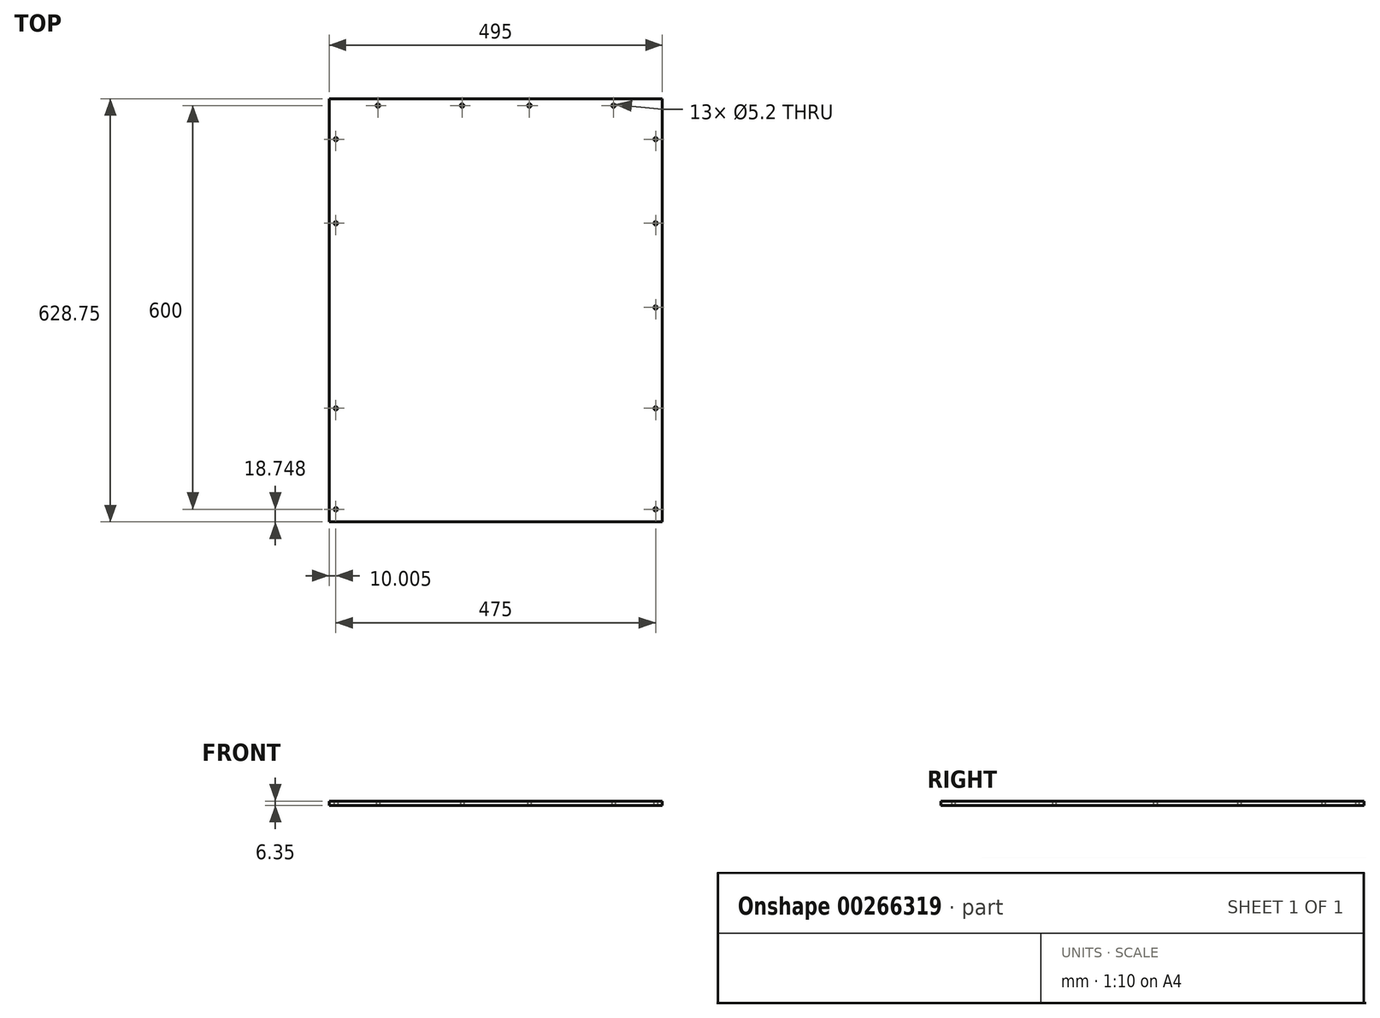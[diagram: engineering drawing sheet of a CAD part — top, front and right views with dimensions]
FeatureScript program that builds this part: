
annotation { "Feature Type Name" : "Feature", "Feature Type Description" : "" }
export const myFeature = defineFeature(function(context is Context, id is Id, definition is map)
    precondition{}
    {
        {
            var Q0;
            Q0=qCreatedBy(makeId("Top.planeOp"),FACE);
            var sketch = newSketch(context, id + "F0", { "sketchPlane" : qUnion([Q0])});
            skLineSegment(sketch, "E0.bottom", {"start": v(-53.27, -32.57) * mm, "end": v(441.73, -32.57) * mm});
            skLineSegment(sketch, "E0.top", {"start": v(-53.27, 596.18) * mm, "end": v(441.73, 596.18) * mm});
            skLineSegment(sketch, "E0.left", {"start": v(-53.27, -32.57) * mm, "end": v(-53.27, 596.18) * mm});
            skLineSegment(sketch, "E0.right", {"start": v(441.73, -32.57) * mm, "end": v(441.73, 596.18) * mm});
            skCircle(sketch, "E1", {"center": v(19.23, 586.18) * mm, "radius": 2.6 * mm});
            skCircle(sketch, "E2", {"center": v(369.23, 586.18) * mm, "radius": 2.6 * mm});
            skCircle(sketch, "E3", {"center": v(144.23, 586.18) * mm, "radius": 2.6 * mm});
            skCircle(sketch, "E4", {"center": v(244.23, 586.18) * mm, "radius": 2.6 * mm});
            skCircle(sketch, "E5", {"center": v(-43.27, 536.18) * mm, "radius": 2.6 * mm});
            skCircle(sketch, "E6", {"center": v(-43.27, 411.18) * mm, "radius": 2.6 * mm});
            skCircle(sketch, "E7", {"center": v(-43.27, 136.18) * mm, "radius": 2.6 * mm});
            skCircle(sketch, "E8", {"center": v(-43.27, -13.82) * mm, "radius": 2.6 * mm});
            skLineSegment(sketch, "E9", {"start": v(194.23, 596.18) * mm, "end": v(194.23, -32.57) * mm});
            skCircle(sketch, "E10.MirrorC", {"center": v(431.73, 536.18) * mm, "radius": 2.6 * mm});
            skCircle(sketch, "E11.MirrorC", {"center": v(431.73, 411.18) * mm, "radius": 2.6 * mm});
            skCircle(sketch, "E12.MirrorC", {"center": v(431.73, 136.18) * mm, "radius": 2.6 * mm});
            skCircle(sketch, "E13.MirrorC", {"center": v(431.73, -13.82) * mm, "radius": 2.6 * mm});
            skCircle(sketch, "E14", {"center": v(431.73, 286.18) * mm, "radius": 2.6 * mm});
            skSolve(sketch);
        }
        {
            var Q0;
            {var subQ0=sQuery(id+"F0.wireOp",EDGE,"E0.left");Q0=makeQuery(id+"F0.imprint","IMPRINT",FACE,{"disambiguationData":[TD([[makeQuery(id+"F0.imprint","IMPRINT",EDGE,{"derivedFrom":subQ0}),-1.0]])]});}
            var Q1;
            {var subQ0=sQuery(id+"F0.wireOp",EDGE,"E0.right");Q1=makeQuery(id+"F0.imprint","IMPRINT",FACE,{"disambiguationData":[TD([[makeQuery(id+"F0.imprint","IMPRINT",EDGE,{"derivedFrom":subQ0}),1.0]])]});}
            extrude(context, id + "F1", {"entities" : qUnion([Q0, Q1]), "depth" : 6.35 * mm});
        }
    });
